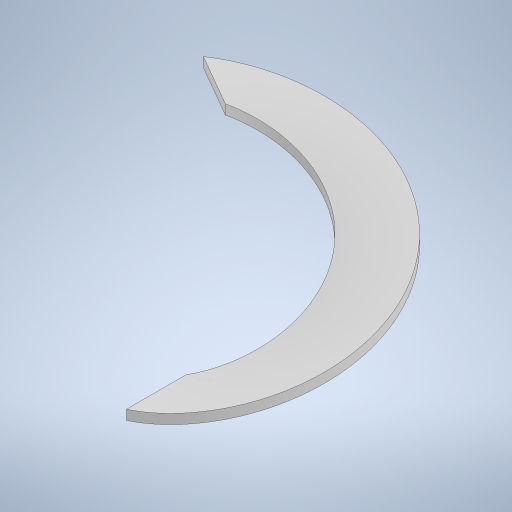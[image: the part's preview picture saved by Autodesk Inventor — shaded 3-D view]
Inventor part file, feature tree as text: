
AUTODESK INVENTOR PART (.ipt)
format: ipt  version: 2024 (Build 280153000, 153)  size: 243,200 bytes
history: native  units: mm
features: sketch x3, plane x1, helix x1
ambient origin geometry x8: Origin, YZ Plane, XZ Plane, XY Plane, X Axis, Y Axis, Z Axis, Center Point
bodies: Solid1 (feature_tree)
feature tree (5):
  sketch  "Sketch1"  dims[d1=6.0mm]
  plane  "Work Plane1"
  sketch  "Sketch2"  dims[d2=150.0mm]
  helix  "Coil1"  [1 undecoded]
  sketch  "Sketch3"  dims[d3=150.0mm d4=150.0mm d5=10.0mm d6=6.666667mm d7=0.0mm d8=90.0deg d9=90.0deg d10=0.0mm d11=0.0mm d12=38.05mm d13=75.0mm d14=6.0mm]
note: 1 required parameter value undecoded (feature->parameter linkage not recoverable at this tier; creation-order binding heuristic only, values carry confidence <= 0.55)
